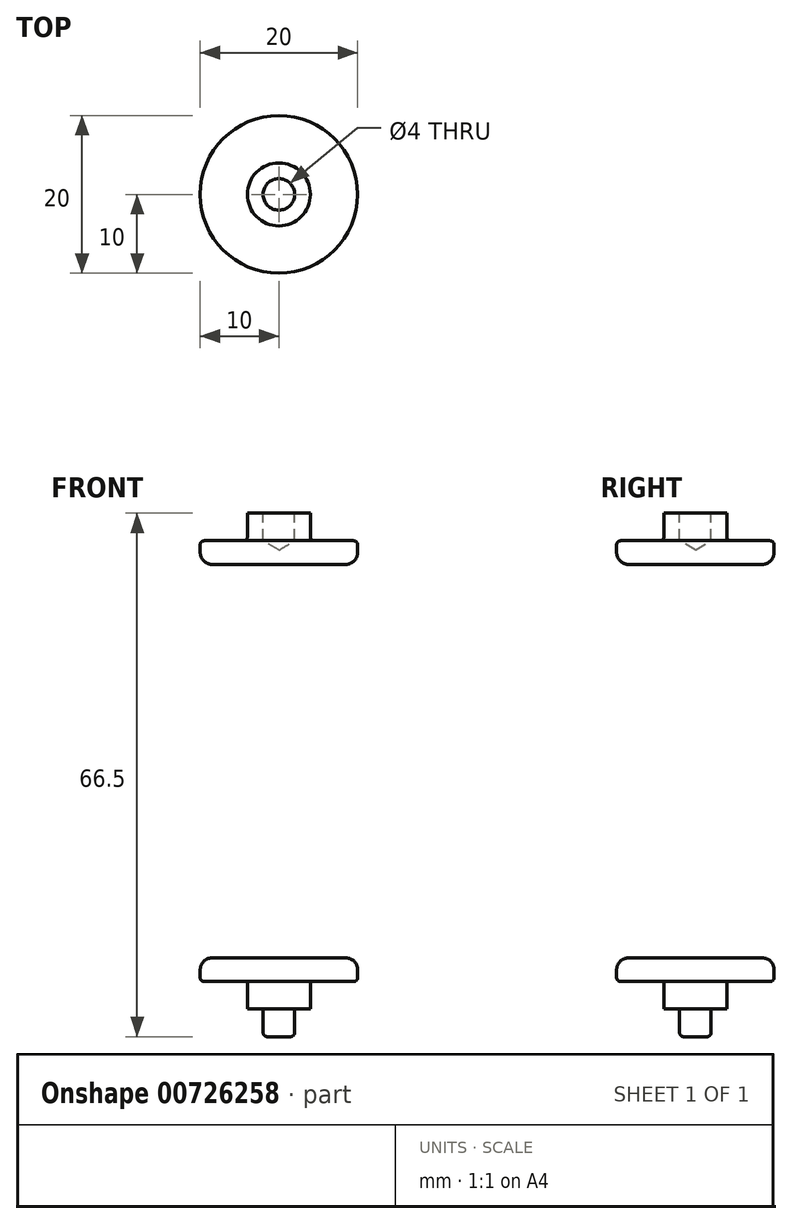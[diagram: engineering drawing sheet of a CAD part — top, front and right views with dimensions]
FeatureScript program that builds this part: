
annotation { "Feature Type Name" : "Feature", "Feature Type Description" : "" }
export const myFeature = defineFeature(function(context is Context, id is Id, definition is map)
    precondition{}
    {
        {
            var Q0;
            Q0=qCreatedBy(makeId("Top.planeOp"),FACE);
            var sketch = newSketch(context, id + "F0", { "sketchPlane" : qUnion([Q0])});
            skCircle(sketch, "E0", {"center": v(0, 0) * mm, "radius": 10 * mm});
            skCircle(sketch, "E1", {"center": v(0, 0) * mm, "radius": 4 * mm});
            skSolve(sketch);
        }
        {
            var Q0;
            Q0 = qSketchRegion(id + "F0", true);
            var Q1;
            Q1=makeQuery(id+"F0.imprint","IMPRINT",FACE,{"disambiguationData":[TD([[makeQuery(id+"F0.imprint","IMPRINT",EDGE,{"derivedFrom":sQuery(id+"F0.wireOp",EDGE,"E1")}),1.0]])]});
            extrude(context, id + "F1", {"entities" : qUnion([Q0, Q1]), "depth" : 3 * mm, "offsetDistance" : 25 * mm});
        }
        {
            var Q0;
            Q0=makeQuery(id+"F0.imprint","IMPRINT",FACE,{"disambiguationData":[TD([[makeQuery(id+"F0.imprint","IMPRINT",EDGE,{"derivedFrom":sQuery(id+"F0.wireOp",EDGE,"E1")}),1.0]])]});
            extrude(context, id + "F2", {"entities" : qUnion([Q0]), "operationType" : NewBodyOperationType.ADD, "oppositeDirection" : true, "depth" : 3.5 * mm, "offsetDistance" : 25 * mm});
        }
        {
            var Q0;
            Q0=makeQuery(id+"F1.opExtrude","CAP_FACE",FACE,{"disambiguationData":[OSD([sQuery(id+"F0.wireOp",EDGE,"E0")])],"isStart":false});
            cPlane(context, id + "F3", {"entities" : qUnion([Q0]), "cplaneType" : CPlaneType.OFFSET, "offset" : 25 * mm, "width" : 150 * mm, "height" : 150 * mm});
        }
        {
            var Q0;
            Q0=makeQuery(id+"F1.opExtrude","SWEPT_BODY",BODY,{"disambiguationData":[OSD([sQuery(id+"F0.wireOp",EDGE,"E0")])]});
            var Q1;
            Q1=qCreatedBy(id+"F3.planeOp",FACE);
            mirror(context, id + "F4", {"entities" : qUnion([Q0]), "mirrorPlane" : qUnion([Q1])});
        }
        {
            var Q0;
            Q0=makeQuery(id+"F2.opExtrude","CAP_FACE",FACE,{"disambiguationData":[OSD([sQuery(id+"F0.wireOp",EDGE,"E1")])],"isStart":false});
            var sketch = newSketch(context, id + "F5", { "sketchPlane" : qUnion([Q0])});
            skCircle(sketch, "E2", {"center": v(0, 0) * mm, "radius": 2 * mm});
            skSolve(sketch);
        }
        {
            var Q0;
            Q0 = qSketchRegion(id + "F5", true);
            extrude(context, id + "F6", {"entities" : qUnion([Q0]), "operationType" : NewBodyOperationType.ADD, "depth" : 3.5 * mm, "offsetDistance" : 25 * mm});
        }
        {
            var Q0;
            Q0=makeQuery(id+"F4.opPattern","COPY",FACE,{"derivedFrom":makeQuery(id+"F2.opExtrude","CAP_FACE",FACE,{"disambiguationData":[OSD([sQuery(id+"F0.wireOp",EDGE,"E1")])],"isStart":false}),"instanceName":"1"});
            var sketch = newSketch(context, id + "F7", { "sketchPlane" : qUnion([Q0])});
            skPoint(sketch, "E3", {"position": v(0, 0) * mm});
            skSolve(sketch);
        }
        {
            var Q0;
            Q0=sQuery(id+"F7.wireOp",VERTEX,"E3");
            var Q1;
            Q1=makeQuery(id+"F4.opPattern","COPY",BODY,{"derivedFrom":makeQuery(id+"F1.opExtrude","SWEPT_BODY",BODY,{"disambiguationData":[OSD([sQuery(id+"F0.wireOp",EDGE,"E0")])]}),"instanceName":"1"});
            hole(context, id + "F8", {"style" : HoleStyle.SIMPLE, "endStyle" : HoleEndStyle.BLIND, "holeDiameter" : 4 * mm, "majorDiameter" : 5 * mm, "holeDepth" : 3.5 * mm, "isTappedThrough" : true, "tappedDepth" : 12 * mm, "tapClearance" : 3, "locations" : qUnion([Q0]), "scope" : qUnion([Q1])});
        }
        {
            var Q0;
            Q0=makeQuery(id+"F8.hole-0.boolean.opBoolean","COPY",EDGE,{"derivedFrom":makeQuery(id+"F8.hole-0.opRevolve","SWEPT_EDGE",EDGE,{"disambiguationData":[OSD([sQuery(id+"F8.hole-0.sketch.wireOp",EDGE,"core_line_2"),sQuery(id+"F8.hole-0.sketch.wireOp",EDGE,"core_line_3")])]})});
            var Q1;
            Q1=makeQuery(id+"F4.opPattern","COPY",FACE,{"derivedFrom":makeQuery(id+"F1.opExtrude","CAP_FACE",FACE,{"disambiguationData":[OSD([sQuery(id+"F0.wireOp",EDGE,"E0")])],"isStart":true}),"instanceName":"1"});
            var Q2;
            Q2=makeQuery(id+"F6.opExtrude","CAP_EDGE",EDGE,{"disambiguationData":[OSD([sQuery(id+"F5.wireOp",EDGE,"E2")])],"isStart":false});
            var Q3;
            Q3=makeQuery(id+"F6.opExtrude","CAP_EDGE",EDGE,{"disambiguationData":[OSD([sQuery(id+"F5.wireOp",EDGE,"E2")])],"isStart":true});
            var Q4;
            Q4=makeQuery(id+"F2.opExtrude","CAP_EDGE",EDGE,{"disambiguationData":[OSD([sQuery(id+"F0.wireOp",EDGE,"E1")])],"isStart":true});
            var Q5;
            Q5=makeQuery(id+"F1.opExtrude","CAP_EDGE",EDGE,{"disambiguationData":[OSD([sQuery(id+"F0.wireOp",EDGE,"E0")])],"isStart":true});
            fillet(context, id + "F9", {"entities" : qUnion([Q0, Q1, Q2, Q3, Q4, Q5]), "radius" : .5 * mm, "tangentPropagation" : true, "allowEdgeOverflow" : false});
        }
        {
            var Q0;
            Q0=makeQuery(id+"F1.opExtrude","CAP_EDGE",EDGE,{"disambiguationData":[OSD([sQuery(id+"F0.wireOp",EDGE,"E0")])],"isStart":false});
            var Q1;
            Q1=makeQuery(id+"F4.opPattern","COPY",EDGE,{"derivedFrom":makeQuery(id+"F1.opExtrude","CAP_EDGE",EDGE,{"disambiguationData":[OSD([sQuery(id+"F0.wireOp",EDGE,"E0")])],"isStart":false}),"instanceName":"1"});
            fillet(context, id + "F10", {"entities" : qUnion([Q0, Q1]), "radius" : 1.5 * mm, "tangentPropagation" : true, "allowEdgeOverflow" : false});
        }
    });
